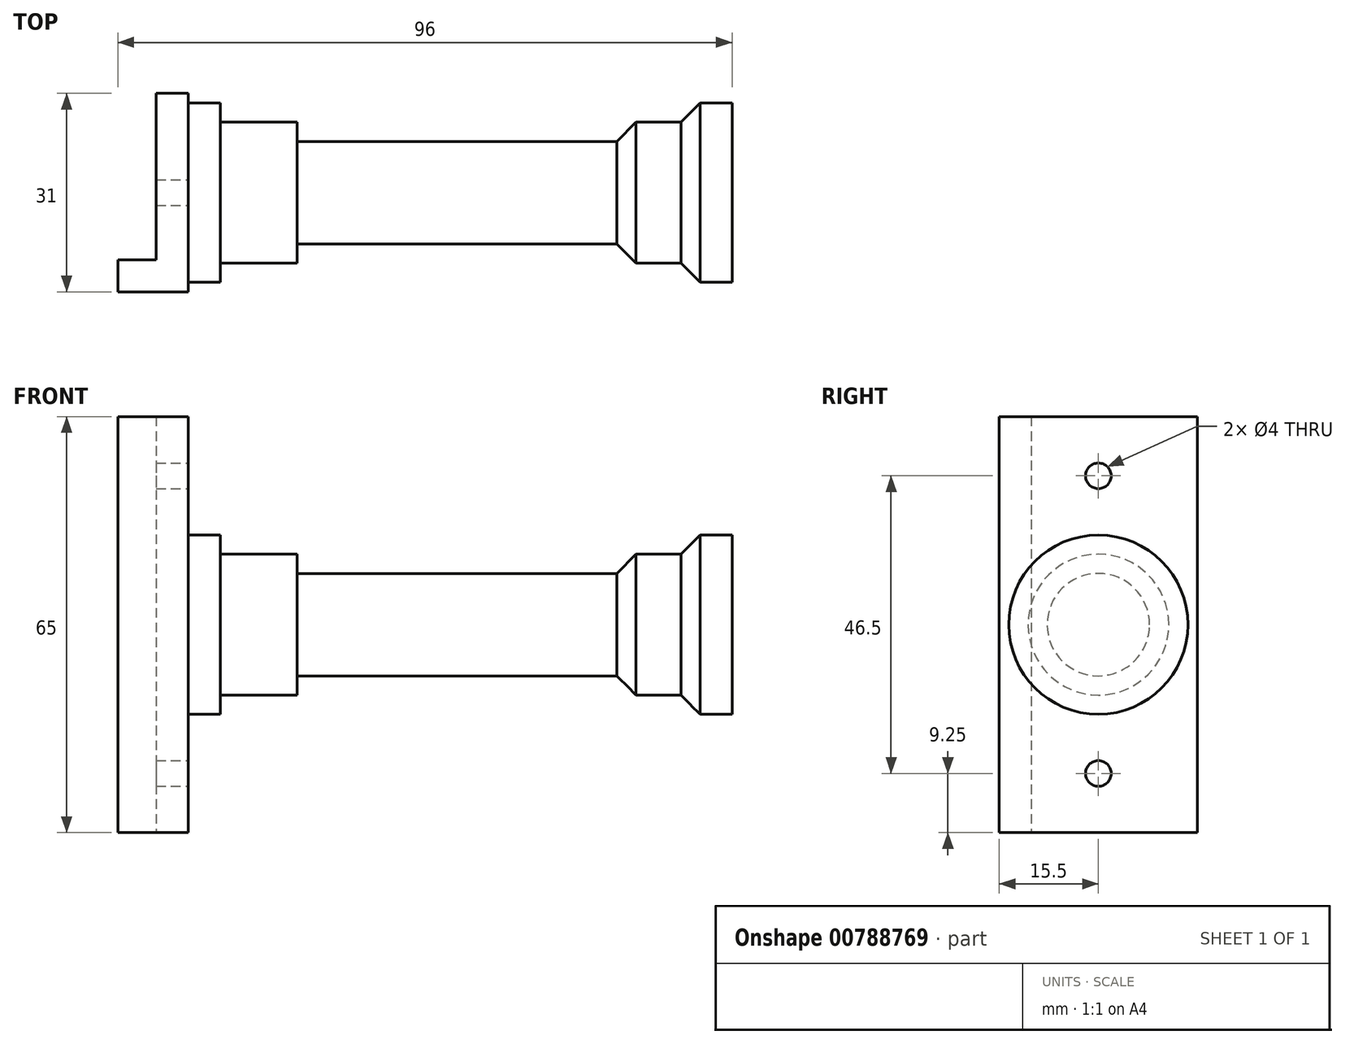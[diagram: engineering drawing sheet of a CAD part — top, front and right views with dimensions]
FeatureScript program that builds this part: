
annotation { "Feature Type Name" : "Feature", "Feature Type Description" : "" }
export const myFeature = defineFeature(function(context is Context, id is Id, definition is map)
    precondition{}
    {
        {
            var Q0;
            Q0=qCreatedBy(makeId("Top.planeOp"),FACE);
            var sketch = newSketch(context, id + "F0", { "sketchPlane" : qUnion([Q0])});
            skLineSegment(sketch, "E0", {"start": v(0, 0) * mm, "end": v(5, 0) * mm});
            skLineSegment(sketch, "E1", {"start": v(5, 0) * mm, "end": v(5, 3) * mm});
            skLineSegment(sketch, "E2", {"start": v(5, 3) * mm, "end": v(17, 3) * mm});
            skLineSegment(sketch, "E3", {"start": v(17, 3) * mm, "end": v(17, 6) * mm});
            skLineSegment(sketch, "E4", {"start": v(65, 6) * mm, "end": v(65, 3) * mm});
            skLineSegment(sketch, "E5", {"start": v(65, 3) * mm, "end": v(75, 3) * mm});
            skLineSegment(sketch, "E6", {"start": v(75, 3) * mm, "end": v(75, 0) * mm});
            skLineSegment(sketch, "E7", {"start": v(75, 0) * mm, "end": v(80, 0) * mm});
            skLineSegment(sketch, "E8", {"start": v(65, 6) * mm, "end": v(65, 14) * mm, "construction": true});
            skLineSegment(sketch, "E9", {"start": v(65, 14) * mm, "end": v(80, 14) * mm});
            skLineSegment(sketch, "E10", {"start": v(80, 14) * mm, "end": v(80, 0) * mm});
            skLineSegment(sketch, "E11", {"start": v(65, 14) * mm, "end": v(0, 14) * mm});
            skLineSegment(sketch, "E12", {"start": v(0, 0) * mm, "end": v(0, 14) * mm});
            skLineSegment(sketch, "E13", {"start": v(17, 6) * mm, "end": v(39, 6) * mm});
            skLineSegment(sketch, "E14", {"start": v(43, 6) * mm, "end": v(65, 6) * mm});
            skLineSegment(sketch, "E15", {"start": v(39, 6) * mm, "end": v(43, 6) * mm});
            skSolve(sketch);
        }
        {
            var Q0;
            Q0=makeQuery(id+"F0.imprint","IMPRINT",FACE,{"disambiguationData":[TD([[makeQuery(id+"F0.imprint","IMPRINT",EDGE,{"derivedFrom":sQuery(id+"F0.wireOp",EDGE,"E0")}),1.0]])]});
            var Q1;
            Q1=sQuery(id+"F0.wireOp",EDGE,"E11");
            revolve(context, id + "F1", {"surfaceOperationType" : NewSurfaceOperationType.NEW, "entities" : qUnion([Q0]), "axis" : qUnion([Q1]), "revolveType" : RevolveType.FULL});
        }
        {
            var Q0;
            Q0=makeQuery(id+"F1.opRevolve","SWEPT_FACE",FACE,{"disambiguationData":[OSD([sQuery(id+"F0.wireOp",EDGE,"E12")])]});
            var sketch = newSketch(context, id + "F2", { "sketchPlane" : qUnion([Q0])});
            skLineSegment(sketch, "E16.bottom", {"start": v(-3.5, -32.5) * mm, "end": v(-24.5, -32.5) * mm});
            skLineSegment(sketch, "E16.top", {"start": v(-3.5, 32.5) * mm, "end": v(-24.5, 32.5) * mm});
            skLineSegment(sketch, "E16.left", {"start": v(-3.5, -32.5) * mm, "end": v(-3.5, 32.5) * mm, "construction": true});
            skLineSegment(sketch, "E16.right", {"start": v(-24.5, -32.5) * mm, "end": v(-24.5, 32.5) * mm, "construction": true});
            skPoint(sketch, "E16.middle", {"position": v(-14, 0) * mm});
            skLineSegment(sketch, "E17", {"start": v(-3.5, -32.5) * mm, "end": v(1.5, -32.5) * mm});
            skLineSegment(sketch, "E18", {"start": v(1.5, -32.5) * mm, "end": v(1.5, 32.5) * mm});
            skLineSegment(sketch, "E19", {"start": v(1.5, 32.5) * mm, "end": v(-3.5, 32.5) * mm});
            skLineSegment(sketch, "E20", {"start": v(-24.5, 32.5) * mm, "end": v(-29.5, 32.5) * mm});
            skLineSegment(sketch, "E21", {"start": v(-29.5, 32.5) * mm, "end": v(-29.5, -32.5) * mm});
            skLineSegment(sketch, "E22", {"start": v(-29.5, -32.5) * mm, "end": v(-24.5, -32.5) * mm});
            skLineSegment(sketch, "E23", {"start": v(-14, 0) * mm, "end": v(-14, 32.5) * mm, "construction": true});
            skLineSegment(sketch, "E24", {"start": v(-14, 32.5) * mm, "end": v(-14, -32.5) * mm, "construction": true});
            skPoint(sketch, "E25", {"position": v(-14, -14) * mm});
            skPoint(sketch, "E26", {"position": v(-14, 14) * mm});
            skLineSegment(sketch, "E27", {"start": v(-14, 14) * mm, "end": v(-14, 23.25) * mm, "construction": true});
            skLineSegment(sketch, "E28", {"start": v(-14, -14) * mm, "end": v(-14, -23.25) * mm, "construction": true});
            skCircle(sketch, "E29", {"center": v(-14, -23.25) * mm, "radius": 2 * mm});
            skCircle(sketch, "E30", {"center": v(-14, 23.25) * mm, "radius": 2 * mm});
            skSolve(sketch);
        }
        {
            var Q0;
            {var subQ0=sQuery(id+"F2.wireOp",EDGE,"E16.top");Q0=makeQuery(id+"F2.imprint","IMPRINT",FACE,{"disambiguationData":[TD([[makeQuery(id+"F2.imprint","IMPRINT",EDGE,{"derivedFrom":subQ0}),1.0]])]});}
            var Q1;
            {var subQ0=sQuery(id+"F2.wireOp",EDGE,"E16.left");var subQ1=makeQuery(id+"F1.opRevolve","SWEPT_EDGE",EDGE,{"disambiguationData":[OSD([sQuery(id+"F0.wireOp",EDGE,"E0"),sQuery(id+"F0.wireOp",EDGE,"E12")])]});var subQ2=makeQuery(id+"F2.imprint","INTERSECT",VERTEX,{"disambiguationData":[OD(0.0)],"derivedFrom":[subQ1,subQ0]});Q1=makeQuery(id+"F2.imprint","IMPRINT",FACE,{"disambiguationData":[TD([[makeQuery(id+"F2.imprint","IMPRINT",EDGE,{"disambiguationData":[TD([[subQ2,-1.0]])],"derivedFrom":subQ0}),1.0]])]});}
            var Q2;
            {var subQ0=sQuery(id+"F2.wireOp",EDGE,"E16.bottom");Q2=makeQuery(id+"F2.imprint","IMPRINT",FACE,{"disambiguationData":[TD([[makeQuery(id+"F2.imprint","IMPRINT",EDGE,{"derivedFrom":subQ0}),-1.0]])]});}
            var Q3;
            Q3=makeQuery(id+"F2.imprint","IMPRINT",FACE,{"disambiguationData":[TD([[makeQuery(id+"F2.imprint","IMPRINT",EDGE,{"derivedFrom":makeQuery(id+"F1.opRevolve","SWEPT_EDGE",EDGE,{"disambiguationData":[OSD([sQuery(id+"F0.wireOp",EDGE,"E0"),sQuery(id+"F0.wireOp",EDGE,"E12")])]})}),-1.0]])]});
            var Q4;
            Q4 = qSketchRegion(id + "F4", true);
            extrude(context, id + "F3", {"entities" : qUnion([Q0, Q1, Q2, Q3, Q4]), "operationType" : NewBodyOperationType.ADD, "depth" : 5 * mm, "offsetDistance" : 25 * mm});
        }
        {
            var Q0;
            Q0=makeQuery(id+"F3.opExtrude","CAP_FACE",FACE,{"disambiguationData":[OSD([sQuery(id+"F2.wireOp",EDGE,"E16.bottom"),sQuery(id+"F2.wireOp",EDGE,"E16.top"),sQuery(id+"F2.wireOp",EDGE,"E17"),sQuery(id+"F2.wireOp",EDGE,"E18"),sQuery(id+"F2.wireOp",EDGE,"E19"),sQuery(id+"F2.wireOp",EDGE,"E20"),sQuery(id+"F2.wireOp",EDGE,"E21"),sQuery(id+"F2.wireOp",EDGE,"E22")])],"isStart":false});
            var sketch = newSketch(context, id + "F4", { "sketchPlane" : qUnion([Q0])});
            skLineSegment(sketch, "E31.bottom", {"start": v(-29.5, -32.5) * mm, "end": v(-24.5, -32.5) * mm});
            skLineSegment(sketch, "E31.top", {"start": v(-29.5, 32.5) * mm, "end": v(-24.5, 32.5) * mm});
            skLineSegment(sketch, "E31.left", {"start": v(-29.5, -32.5) * mm, "end": v(-29.5, 32.5) * mm});
            skLineSegment(sketch, "E31.right", {"start": v(-24.5, -32.5) * mm, "end": v(-24.5, 32.5) * mm});
            skLineSegment(sketch, "E32.bottom", {"start": v(1.5, 32.5) * mm, "end": v(-3.5, 32.5) * mm});
            skLineSegment(sketch, "E32.top", {"start": v(1.5, -32.5) * mm, "end": v(-3.5, -32.5) * mm});
            skLineSegment(sketch, "E32.left", {"start": v(1.5, 32.5) * mm, "end": v(1.5, -32.5) * mm});
            skLineSegment(sketch, "E32.right", {"start": v(-3.5, 32.5) * mm, "end": v(-3.5, -32.5) * mm});
            skSolve(sketch);
        }
        {
            var Q0;
            Q0=makeQuery(id+"F4.imprint","IMPRINT",FACE,{"disambiguationData":[TD([[makeQuery(id+"F4.imprint","IMPRINT",EDGE,{"derivedFrom":sQuery(id+"F4.wireOp",EDGE,"E32.bottom")}),1.0]])]});
            var Q1;
            Q1=makeQuery(id+"F4.imprint","IMPRINT",FACE,{"disambiguationData":[TD([[makeQuery(id+"F4.imprint","IMPRINT",EDGE,{"derivedFrom":sQuery(id+"F4.wireOp",EDGE,"E31.bottom")}),1.0]])]});
            extrude(context, id + "F5", {"entities" : qUnion([Q0, Q1]), "operationType" : NewBodyOperationType.ADD, "depth" : 6 * mm, "offsetDistance" : 25 * mm});
        }
        {
            var Q0;
            Q0=makeQuery(id+"F1.opRevolve","SWEPT_EDGE",EDGE,{"disambiguationData":[OSD([sQuery(id+"F0.wireOp",EDGE,"E4"),sQuery(id+"F0.wireOp",EDGE,"E5")])]});
            var Q1;
            Q1=makeQuery(id+"F1.opRevolve","SWEPT_EDGE",EDGE,{"disambiguationData":[OSD([sQuery(id+"F0.wireOp",EDGE,"E6"),sQuery(id+"F0.wireOp",EDGE,"E7")])]});
            chamfer(context, id + "F6", {"entities" : qUnion([Q0, Q1]), "width" : 5 * mm, "tangentPropagation" : true});
        }
        {
            var Q0;
            Q0=makeQuery(id+"F1.opRevolve","SWEPT_FACE",FACE,{"disambiguationData":[OSD([sQuery(id+"F0.wireOp",EDGE,"E10")])]});
            extrude(context, id + "F7", {"entities" : qUnion([Q0]), "operationType" : NewBodyOperationType.ADD, "depth" : 5 * mm, "offsetDistance" : 25 * mm});
        }
    });
